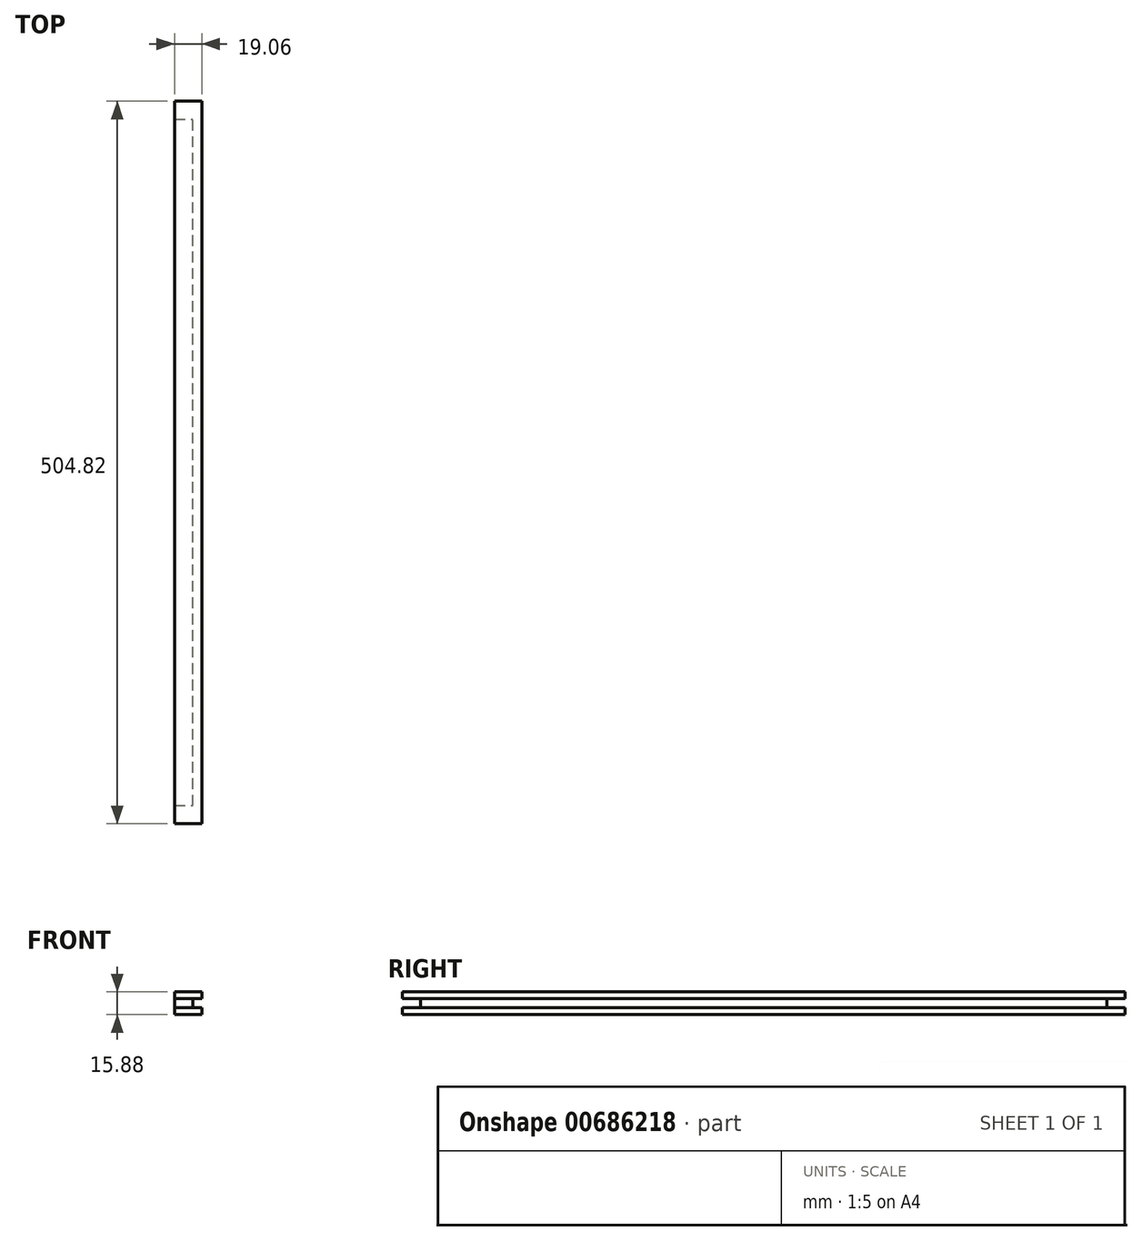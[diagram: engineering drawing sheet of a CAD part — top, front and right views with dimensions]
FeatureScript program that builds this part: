
annotation { "Feature Type Name" : "Feature", "Feature Type Description" : "" }
export const myFeature = defineFeature(function(context is Context, id is Id, definition is map)
    precondition{}
    {
        {
            var Q0;
            Q0=qCreatedBy(makeId("Front.planeOp"),FACE);
            var sketch = newSketch(context, id + "F0", { "sketchPlane" : qUnion([Q0])});
            skLineSegment(sketch, "E0.bottom", {"start": v(-9.53, 7.94) * mm, "end": v(9.52, 7.94) * mm});
            skLineSegment(sketch, "E0.top", {"start": v(-9.53, -7.94) * mm, "end": v(9.52, -7.94) * mm});
            skLineSegment(sketch, "E0.left", {"start": v(-9.53, 7.94) * mm, "end": v(-9.53, -7.94) * mm});
            skLineSegment(sketch, "E0.right", {"start": v(9.52, 7.94) * mm, "end": v(9.52, 3.18) * mm});
            skPoint(sketch, "E0.middle", {"position": v(0, 0) * mm});
            skLineSegment(sketch, "E1", {"start": v(9.52, 3.18) * mm, "end": v(3.17, 3.18) * mm});
            skLineSegment(sketch, "E2", {"start": v(3.17, 3.18) * mm, "end": v(3.17, -3.18) * mm});
            skLineSegment(sketch, "E3", {"start": v(3.17, -3.18) * mm, "end": v(9.52, -3.17) * mm});
            skLineSegment(sketch, "E4", {"start": v(0, 0) * mm, "end": v(3.17, 0) * mm, "construction": true});
            skLineSegment(sketch, "E5.trimOffspring", {"start": v(9.52, -3.17) * mm, "end": v(9.52, -7.94) * mm});
            skSolve(sketch);
        }
        {
            var Q0;
            Q0 = qSketchRegion(id + "F0", true);
            extrude(context, id + "F1", {"entities" : qUnion([Q0]), "endBound" : BoundingType.SYMMETRIC, "depth" : 504.82 * mm, "offsetDistance" : 25.4 * mm});
        }
        {
            var Q0;
            Q0=qCreatedBy(makeId("Right.planeOp"),FACE);
            var sketch = newSketch(context, id + "F2", { "sketchPlane" : qUnion([Q0])});
            skLineSegment(sketch, "E6.bottom", {"start": v(-239.71, -3.17) * mm, "end": v(-252.41, -3.17) * mm});
            skLineSegment(sketch, "E6.top", {"start": v(-239.71, 3.18) * mm, "end": v(-252.41, 3.17) * mm});
            skLineSegment(sketch, "E6.left", {"start": v(-239.71, -3.17) * mm, "end": v(-239.71, 3.18) * mm});
            skLineSegment(sketch, "E6.right", {"start": v(-252.41, -3.17) * mm, "end": v(-252.41, 3.18) * mm});
            skLineSegment(sketch, "E7", {"start": v(0, 21.45) * mm, "end": v(0, -22.74) * mm, "construction": true});
            skLineSegment(sketch, "E8.MirrorCS", {"start": v(252.41, -3.17) * mm, "end": v(252.41, 3.18) * mm});
            skLineSegment(sketch, "E9.MirrorCS", {"start": v(239.71, -3.17) * mm, "end": v(239.71, 3.18) * mm});
            skLineSegment(sketch, "E10.MirrorCS", {"start": v(239.71, 3.18) * mm, "end": v(252.41, 3.17) * mm});
            skLineSegment(sketch, "E11.MirrorCS", {"start": v(239.71, -3.17) * mm, "end": v(252.41, -3.17) * mm});
            skSolve(sketch);
        }
        {
            var Q0;
            Q0 = qSketchRegion(id + "F2", true);
            extrude(context, id + "F3", {"entities" : qUnion([Q0]), "operationType" : NewBodyOperationType.REMOVE, "endBound" : BoundingType.THROUGH_ALL, "oppositeDirection" : true, "depth" : 25.4 * mm, "offsetDistance" : 25.4 * mm, "hasSecondDirection" : true, "secondDirectionBound" : SecondDirectionBoundingType.THROUGH_ALL, "secondDirectionOppositeDirection" : false, "secondDirectionDepth" : 25.4 * mm});
        }
    });
